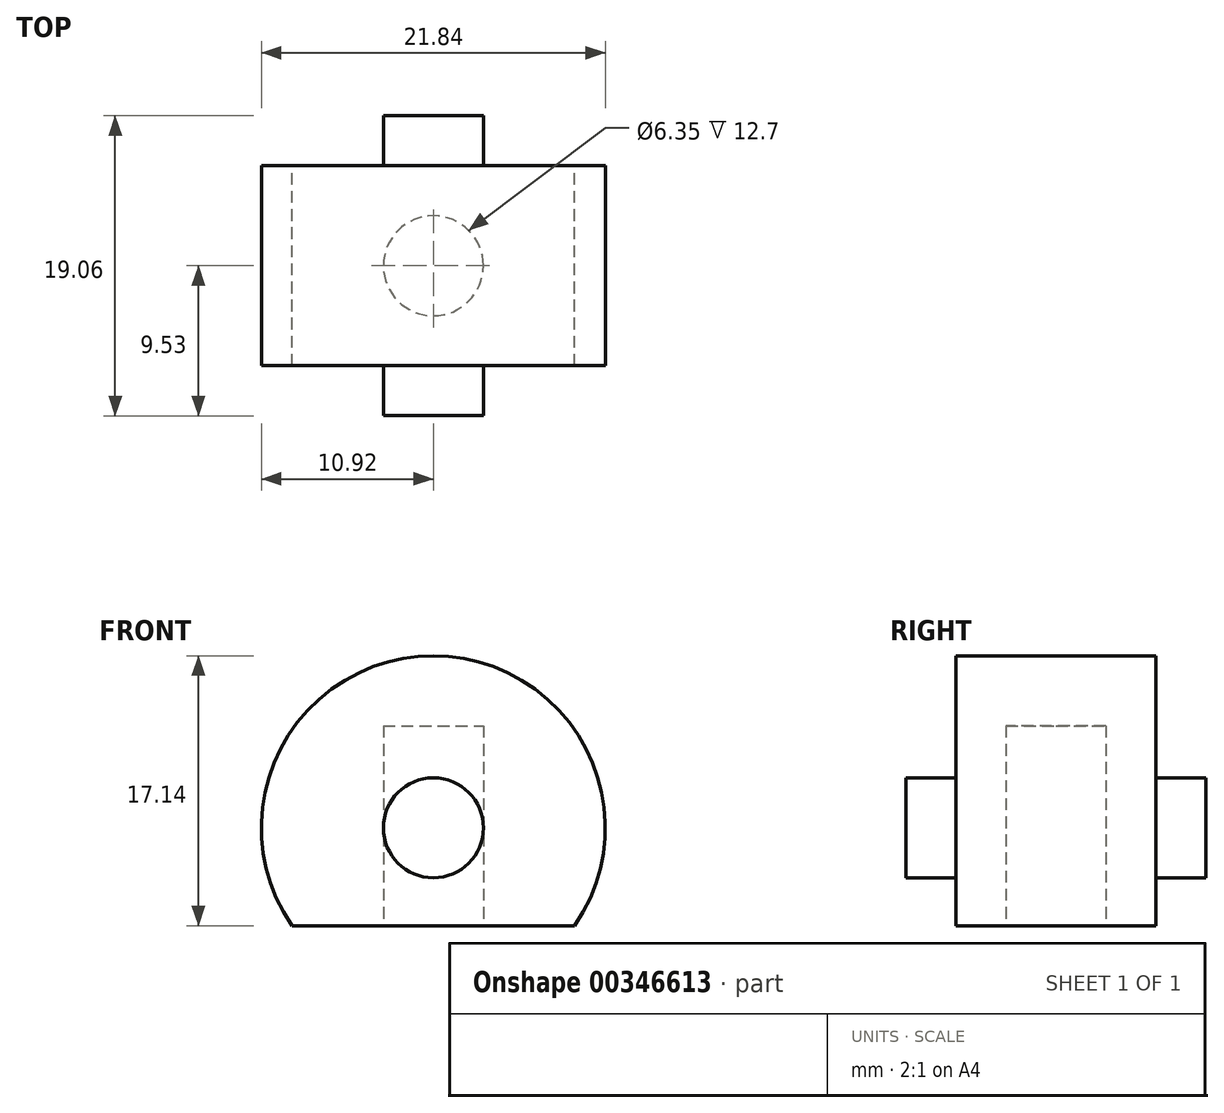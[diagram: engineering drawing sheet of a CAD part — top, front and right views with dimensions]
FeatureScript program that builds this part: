
annotation { "Feature Type Name" : "Feature", "Feature Type Description" : "" }
export const myFeature = defineFeature(function(context is Context, id is Id, definition is map)
    precondition{}
    {
        {
            var Q0;
            Q0=qCreatedBy(makeId("Front.planeOp"),FACE);
            var sketch = newSketch(context, id + "F0", { "sketchPlane" : qUnion([Q0])});
            skArc(sketch, "E0", {"start": v(8.98, -6.22) * mm, "mid": v(0, 10.92) * mm, "end": v(-8.98, -6.22) * mm});
            skLineSegment(sketch, "E1", {"start": v(-8.98, -6.22) * mm, "end": v(8.98, -6.22) * mm});
            skSolve(sketch);
        }
        {
            var Q0;
            Q0 = qSketchRegion(id + "F0", true);
            extrude(context, id + "F1", {"entities" : qUnion([Q0]), "depth" : 12.7 * mm});
        }
        {
            var Q0;
            Q0=makeQuery(id+"F1.opExtrude","CAP_FACE",FACE,{"disambiguationData":[OSD([sQuery(id+"F0.wireOp",EDGE,"E0"),sQuery(id+"F0.wireOp",EDGE,"E1")])],"isStart":false});
            var sketch = newSketch(context, id + "F2", { "sketchPlane" : qUnion([Q0])});
            skArc(sketch, "E2.0", {"start": v(8.98, -6.22) * mm, "mid": v(0, 10.92) * mm, "end": v(-8.98, -6.22) * mm});
            skCircle(sketch, "E3", {"center": v(0, 0) * mm, "radius": 3.18 * mm});
            skSolve(sketch);
        }
        {
            var Q0;
            Q0 = qSketchRegion(id + "F2", true);
            extrude(context, id + "F3", {"entities" : qUnion([Q0]), "operationType" : NewBodyOperationType.ADD, "depth" : 3.17 * mm});
        }
        {
            var Q0;
            Q0=makeQuery(id+"F1.opExtrude","CAP_FACE",FACE,{"disambiguationData":[OSD([sQuery(id+"F0.wireOp",EDGE,"E0"),sQuery(id+"F0.wireOp",EDGE,"E1")])],"isStart":true});
            var sketch = newSketch(context, id + "F4", { "sketchPlane" : qUnion([Q0])});
            skCircle(sketch, "E4", {"center": v(0, 0) * mm, "radius": 3.17 * mm});
            skSolve(sketch);
        }
        {
            var Q0;
            Q0 = qSketchRegion(id + "F4", true);
            extrude(context, id + "F5", {"entities" : qUnion([Q0]), "operationType" : NewBodyOperationType.ADD, "depth" : 3.17 * mm});
        }
        {
            var Q0;
            Q0=makeQuery(id+"F1.opExtrude","SWEPT_FACE",FACE,{"disambiguationData":[OSD([sQuery(id+"F0.wireOp",EDGE,"E1")])]});
            var sketch = newSketch(context, id + "F6", { "sketchPlane" : qUnion([Q0])});
            skCircle(sketch, "E5", {"center": v(0, 6.35) * mm, "radius": 3.18 * mm});
            skSolve(sketch);
        }
        {
            var Q0;
            Q0 = qSketchRegion(id + "F6", true);
            extrude(context, id + "F7", {"entities" : qUnion([Q0]), "operationType" : NewBodyOperationType.REMOVE, "oppositeDirection" : true, "depth" : 12.7 * mm});
        }
    });
